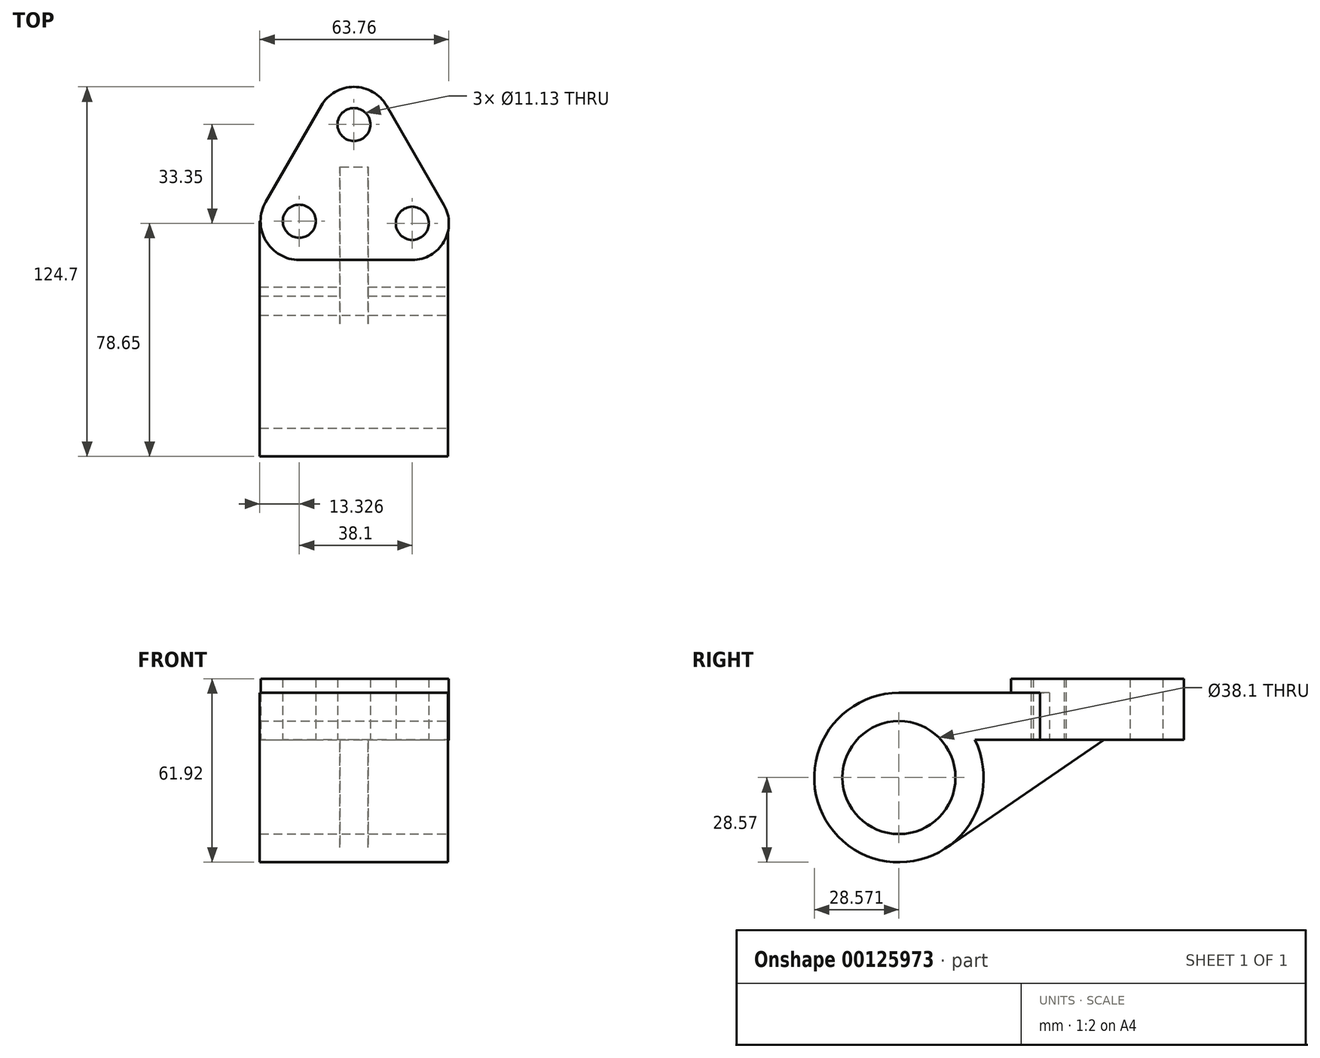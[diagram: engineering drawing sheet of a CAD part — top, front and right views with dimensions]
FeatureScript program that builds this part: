
annotation { "Feature Type Name" : "Feature", "Feature Type Description" : "" }
export const myFeature = defineFeature(function(context is Context, id is Id, definition is map)
    precondition{}
    {
        {
            var Q0;
            Q0=qCreatedBy(makeId("Top.planeOp"),FACE);
            var sketch = newSketch(context, id + "F0", { "sketchPlane" : qUnion([Q0])});
            skCircle(sketch, "E0.cCircle", {"center": v(0, 0) * mm, "radius": 23.7 * mm, "construction": true});
            skLineSegment(sketch, "E0.0", {"start": v(19.68, -23.7) * mm, "end": v(-18.42, -23.7) * mm});
            skLineSegment(sketch, "E0.1", {"start": v(-29.73, -4.1) * mm, "end": v(-11, 28.34) * mm});
            skLineSegment(sketch, "E0.2", {"start": v(11, 28.34) * mm, "end": v(30.36, -5.2) * mm});
            skPoint(sketch, "E0.0.midPoint", {"position": v(0, -23.7) * mm});
            skPoint(sketch, "E1.visualSharp", {"position": v(0, 47.4) * mm});
            skArc(sketch, "E1.filletArc", {"start": v(11, 28.34) * mm, "mid": v(0, 34.7) * mm, "end": v(-11, 28.34) * mm});
            skPoint(sketch, "E2.visualSharp", {"position": v(-41.04, -23.7) * mm});
            skArc(sketch, "E2.filletArc", {"start": v(-29.73, -4.1) * mm, "mid": v(-29.73, -17.17) * mm, "end": v(-18.42, -23.7) * mm});
            skPoint(sketch, "E3.visualSharp", {"position": v(41.04, -23.7) * mm});
            skArc(sketch, "E3.filletArc", {"start": v(19.68, -23.7) * mm, "mid": v(30.36, -17.53) * mm, "end": v(30.36, -5.2) * mm});
            skCircle(sketch, "E4", {"center": v(-18.42, -10.64) * mm, "radius": 5.56 * mm});
            skCircle(sketch, "E5", {"center": v(19.68, -11.36) * mm, "radius": 5.56 * mm});
            skCircle(sketch, "E6", {"center": v(0, 22) * mm, "radius": 5.56 * mm});
            skSolve(sketch);
        }
        {
            var Q0;
            Q0 = qSketchRegion(id + "F0", true);
            extrude(context, id + "F1", {"entities" : qUnion([Q0]), "depth" : 20.65 * mm});
        }
        {
            var Q0;
            Q0=makeQuery(id+"F1.opExtrude","SWEPT_FACE",FACE,{"disambiguationData":[OSD([sQuery(id+"F0.wireOp",EDGE,"E0.0")])]});
            var sketch = newSketch(context, id + "F2", { "sketchPlane" : qUnion([Q0])});
            skLineSegment(sketch, "E7.bottom", {"start": v(-31.75, 0) * mm, "end": v(31.75, 0) * mm});
            skLineSegment(sketch, "E7.top", {"start": v(-31.75, 15.87) * mm, "end": v(31.75, 15.87) * mm});
            skLineSegment(sketch, "E7.left", {"start": v(-31.75, 0) * mm, "end": v(-31.75, 15.88) * mm});
            skLineSegment(sketch, "E7.right", {"start": v(31.75, 0) * mm, "end": v(31.75, 15.88) * mm});
            skLineSegment(sketch, "E8", {"start": v(0, 15.87) * mm, "end": v(0, 0) * mm, "construction": true});
            skSolve(sketch);
        }
        {
            var Q0;
            Q0 = qSketchRegion(id + "F2", true);
            extrude(context, id + "F3", {"entities" : qUnion([Q0]), "operationType" : NewBodyOperationType.ADD, "depth" : 37.74 * mm, "hasSecondDirection" : true, "secondDirectionOppositeDirection" : true, "secondDirectionDepth" : 13.06 * mm});
        }
        {
            var Q0;
            Q0=makeQuery(id+"F1.opExtrude","CAP_FACE",FACE,{"disambiguationData":[OSD([sQuery(id+"F0.wireOp",EDGE,"E0.0"),sQuery(id+"F0.wireOp",EDGE,"E0.1"),sQuery(id+"F0.wireOp",EDGE,"E0.2"),sQuery(id+"F0.wireOp",EDGE,"E1.filletArc"),sQuery(id+"F0.wireOp",EDGE,"E2.filletArc"),sQuery(id+"F0.wireOp",EDGE,"E3.filletArc"),sQuery(id+"F0.wireOp",EDGE,"E4"),sQuery(id+"F0.wireOp",EDGE,"E5"),sQuery(id+"F0.wireOp",EDGE,"E6")])],"isStart":false});
            var sketch = newSketch(context, id + "F4", { "sketchPlane" : qUnion([Q0])});
            skCircle(sketch, "E9.0", {"center": v(-18.42, -10.64) * mm, "radius": 5.56 * mm});
            skCircle(sketch, "E9.1", {"center": v(19.68, -11.36) * mm, "radius": 5.56 * mm});
            skSolve(sketch);
        }
        {
            var Q0;
            Q0 = qSketchRegion(id + "F4", true);
            extrude(context, id + "F5", {"entities" : qUnion([Q0]), "operationType" : NewBodyOperationType.REMOVE, "endBound" : BoundingType.THROUGH_ALL, "oppositeDirection" : true, "depth" : 25.4 * mm});
        }
        {
            var Q0;
            Q0=makeQuery(id+"F3.opExtrude","SWEPT_FACE",FACE,{"disambiguationData":[OSD([sQuery(id+"F2.wireOp",EDGE,"E7.right")])]});
            var sketch = newSketch(context, id + "F6", { "sketchPlane" : qUnion([Q0])});
            skArc(sketch, "E10", {"start": v(-61.44, 15.88) * mm, "mid": v(-76.5, -36.98) * mm, "end": v(-35.84, 0) * mm});
            skCircle(sketch, "E11", {"center": v(-61.44, -12.7) * mm, "radius": 19.05 * mm});
            skSolve(sketch);
        }
        {
            var Q0;
            {var subQ0=sQuery(id+"F6.wireOp",EDGE,"E10");Q0=makeQuery(id+"F6.imprint","IMPRINT",FACE,{"disambiguationData":[TD([[makeQuery(id+"F6.imprint","IMPRINT",EDGE,{"derivedFrom":subQ0}),1.0]])]});}
            var Q1;
            Q1=makeQuery(id+"F3.opExtrude","SWEPT_FACE",FACE,{"disambiguationData":[OSD([sQuery(id+"F2.wireOp",EDGE,"E7.left")])]});
            extrude(context, id + "F7", {"entities" : qUnion([Q0]), "operationType" : NewBodyOperationType.ADD, "endBound" : BoundingType.UP_TO_SURFACE, "oppositeDirection" : true, "endBoundEntityFace" : qUnion([Q1]), "depth" : 25.4 * mm});
        }
        {
            var Q0;
            {var subQ0=sQuery(id+"F6.wireOp",EDGE,"E11");var subQ1=sQuery(id+"F2.wireOp",EDGE,"E7.right");var subQ2=makeQuery(id+"F3.opExtrude","CAP_EDGE",EDGE,{"disambiguationData":[OSD([subQ1])],"isStart":false});var subQ3=makeQuery(id+"F6.imprint","INTERSECT",VERTEX,{"derivedFrom":[subQ2,subQ0]});Q0=makeQuery(id+"F6.imprint","IMPRINT",FACE,{"disambiguationData":[TD([[makeQuery(id+"F6.imprint","IMPRINT",EDGE,{"disambiguationData":[TD([[subQ3,1.0]])],"derivedFrom":subQ0}),1.0]])]});}
            extrude(context, id + "F8", {"entities" : qUnion([Q0]), "operationType" : NewBodyOperationType.REMOVE, "endBound" : BoundingType.THROUGH_ALL, "oppositeDirection" : true, "depth" : 25.4 * mm});
        }
        {
            var Q0;
            {var subQ1=sQuery(id+"F0.wireOp",EDGE,"E0.2");var subQ2=sQuery(id+"F0.wireOp",EDGE,"E5");var subQ3=sQuery(id+"F0.wireOp",EDGE,"E4");var subQ4=sQuery(id+"F0.wireOp",EDGE,"E3.filletArc");var subQ5=sQuery(id+"F0.wireOp",EDGE,"E6");var subQ6=sQuery(id+"F0.wireOp",EDGE,"E0.1");var subQ8=sQuery(id+"F2.wireOp",EDGE,"E7.bottom");var subQ9=sQuery(id+"F0.wireOp",EDGE,"E1.filletArc");var subQ11=sQuery(id+"F0.wireOp",EDGE,"E2.filletArc");Q0=makeQuery(id+"F7.boolean.opBoolean","SPLIT",FACE,{"disambiguationData":[TD([makeQuery(id+"F1.opExtrude","SWEPT_FACE",FACE,{"disambiguationData":[OSD([subQ6])]})])],"derivedFrom":makeQuery(id+"F3.boolean.opBoolean","MERGE",FACE,{"derivedFrom":[makeQuery(id+"F1.opExtrude","CAP_FACE",FACE,{"disambiguationData":[OSD([sQuery(id+"F0.wireOp",EDGE,"E0.0"),subQ6,subQ1,subQ9,subQ11,subQ4,subQ3,subQ2,subQ5])],"isStart":true}),makeQuery(id+"F3.opExtrude","SWEPT_FACE",FACE,{"disambiguationData":[OSD([subQ8])]})]})});}
            var sketch = newSketch(context, id + "F9", { "sketchPlane" : qUnion([Q0])});
            skCircle(sketch, "E12.0", {"center": v(19.68, 11.36) * mm, "radius": 5.56 * mm, "construction": true});
            skCircle(sketch, "E12.1", {"center": v(-18.42, 10.64) * mm, "radius": 5.56 * mm, "construction": true});
            skLineSegment(sketch, "E13", {"start": v(0, 0) * mm, "end": v(0, -7.69) * mm, "construction": true});
            skLineSegment(sketch, "E14", {"start": v(0, -7.69) * mm, "end": v(-4.76, -7.69) * mm});
            skLineSegment(sketch, "E15", {"start": v(0, -7.69) * mm, "end": v(4.76, -7.69) * mm});
            skLineSegment(sketch, "E16", {"start": v(-4.76, -7.69) * mm, "end": v(-4.76, 35.84) * mm});
            skLineSegment(sketch, "E17", {"start": v(4.76, -7.69) * mm, "end": v(4.76, 35.84) * mm});
            skLineSegment(sketch, "E18", {"start": v(4.76, 35.84) * mm, "end": v(-4.76, 35.84) * mm});
            skSolve(sketch);
        }
        {
            var Q0;
            {var subQ0=sQuery(id+"F2.wireOp",EDGE,"E7.right");Q0=makeQuery(id+"F7.boolean.opBoolean","MERGE",FACE,{"derivedFrom":[makeQuery(id+"F3.opExtrude","SWEPT_FACE",FACE,{"disambiguationData":[OSD([subQ0])]}),makeQuery(id+"F7.opExtrude","CAP_FACE",FACE,{"disambiguationData":[OSD([sQuery(id+"F2.wireOp",EDGE,"E7.bottom"),subQ0,sQuery(id+"F6.wireOp",EDGE,"E10"),sQuery(id+"F6.wireOp",EDGE,"E11")])],"isStart":true})]});}
            var sketch = newSketch(context, id + "F10", { "sketchPlane" : qUnion([Q0])});
            skLineSegment(sketch, "E19", {"start": v(7.69, 0) * mm, "end": v(-45.3, -36.28) * mm});
            skLineSegment(sketch, "E20", {"start": v(-45.3, -36.28) * mm, "end": v(-35.84, 0) * mm});
            skLineSegment(sketch, "E21", {"start": v(-35.84, 0) * mm, "end": v(7.69, 0) * mm});
            skSolve(sketch);
        }
        {
            var Q0;
            Q0 = qSketchRegion(id + "F10", true);
            extrude(context, id + "F11", {"entities" : qUnion([Q0]), "operationType" : NewBodyOperationType.ADD, "oppositeDirection" : true, "depth" : 36.5 * mm, "hasSecondDirection" : true, "secondDirectionOppositeDirection" : true, "secondDirectionDepth" : 26.99 * mm});
        }
    });
